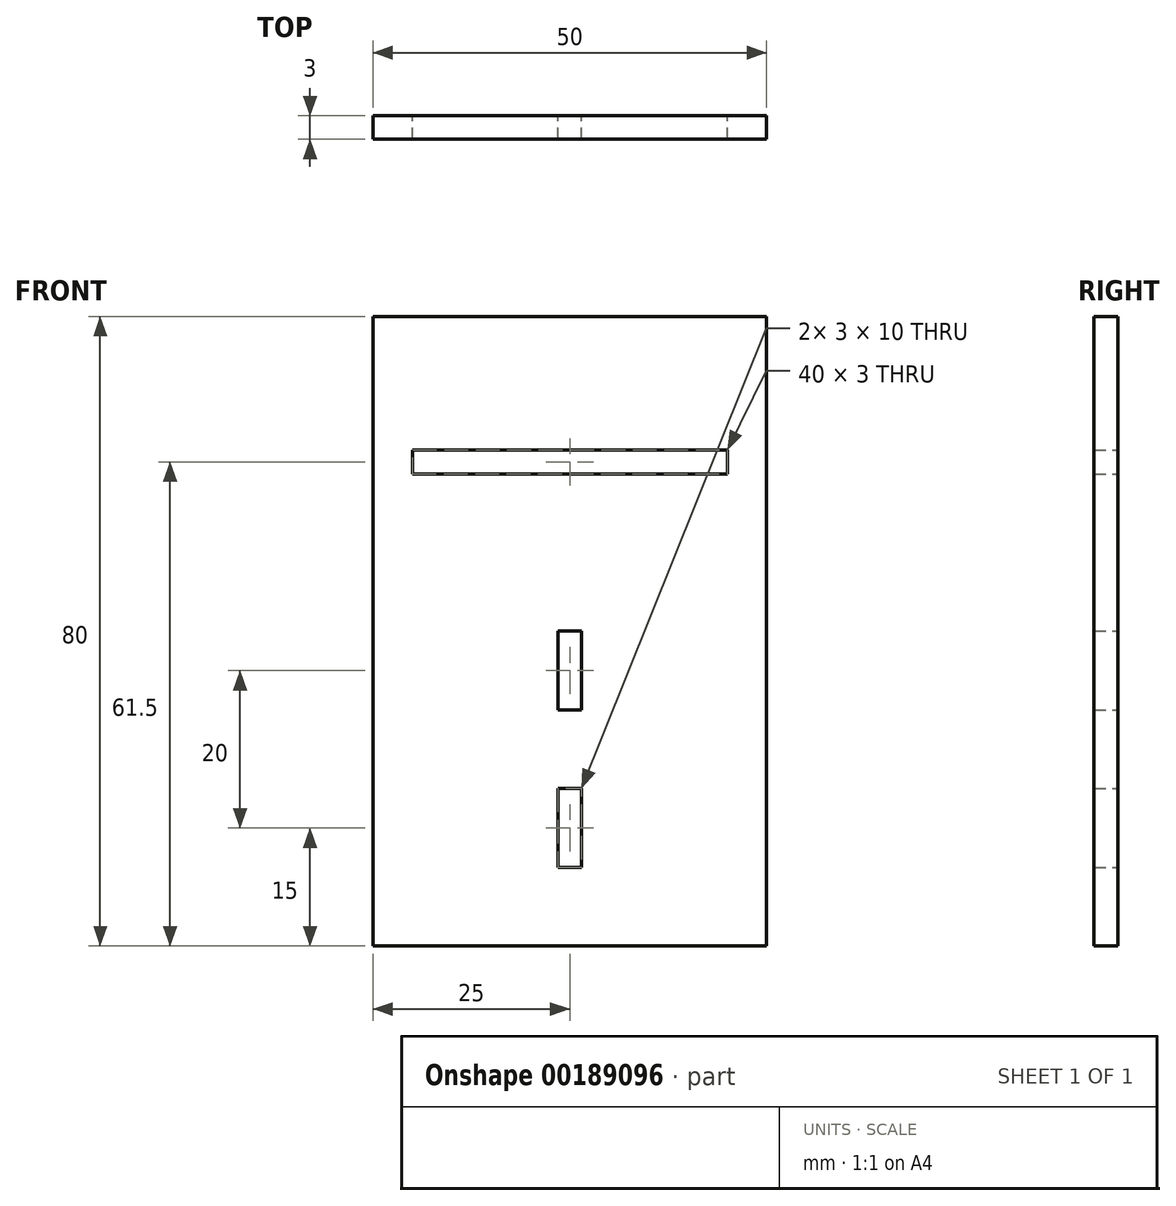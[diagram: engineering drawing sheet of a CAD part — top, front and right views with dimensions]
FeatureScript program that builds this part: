
annotation { "Feature Type Name" : "Feature", "Feature Type Description" : "" }
export const myFeature = defineFeature(function(context is Context, id is Id, definition is map)
    precondition{}
    {
        {
            var Q0;
            Q0=qCreatedBy(makeId("Front.planeOp"),FACE);
            var sketch = newSketch(context, id + "F1", { "sketchPlane" : qUnion([Q0])});
            skLineSegment(sketch, "E0.bottom", {"start": v(25, 40) * mm, "end": v(-25, 40) * mm});
            skLineSegment(sketch, "E0.top", {"start": v(25, -40) * mm, "end": v(-25, -40) * mm});
            skLineSegment(sketch, "E0.left", {"start": v(25, 40) * mm, "end": v(25, -40) * mm});
            skLineSegment(sketch, "E0.right", {"start": v(-25, 40) * mm, "end": v(-25, -40) * mm});
            skPoint(sketch, "E0.middle", {"position": v(0, 0) * mm});
            skLineSegment(sketch, "E1.bottom", {"start": v(20, 23) * mm, "end": v(-20, 23) * mm});
            skLineSegment(sketch, "E1.top", {"start": v(20, 20) * mm, "end": v(-20, 20) * mm});
            skLineSegment(sketch, "E1.left", {"start": v(20, 23) * mm, "end": v(20, 20) * mm});
            skLineSegment(sketch, "E1.right", {"start": v(-20, 23) * mm, "end": v(-20, 20) * mm});
            skPoint(sketch, "E1.middle", {"position": v(0, 21.5) * mm});
            skLineSegment(sketch, "E2.bottom", {"start": v(1.5, 0) * mm, "end": v(-1.5, 0) * mm});
            skLineSegment(sketch, "E2.top", {"start": v(1.5, -10) * mm, "end": v(-1.5, -10) * mm});
            skLineSegment(sketch, "E2.left", {"start": v(1.5, 0) * mm, "end": v(1.5, -10) * mm});
            skLineSegment(sketch, "E2.right", {"start": v(-1.5, 0) * mm, "end": v(-1.5, -10) * mm});
            skPoint(sketch, "E2.middle", {"position": v(0, -5) * mm});
            skLineSegment(sketch, "E3.bottom", {"start": v(1.5, -20) * mm, "end": v(-1.5, -20) * mm});
            skLineSegment(sketch, "E3.top", {"start": v(1.5, -30) * mm, "end": v(-1.5, -30) * mm});
            skLineSegment(sketch, "E3.left", {"start": v(1.5, -20) * mm, "end": v(1.5, -30) * mm});
            skLineSegment(sketch, "E3.right", {"start": v(-1.5, -20) * mm, "end": v(-1.5, -30) * mm});
            skPoint(sketch, "E3.middle", {"position": v(0, -25) * mm});
            skSolve(sketch);
        }
        {
            var Q0;
            Q0=makeQuery(id+"F1.imprint","IMPRINT",FACE,{"disambiguationData":[TD([[makeQuery(id+"F1.imprint","IMPRINT",EDGE,{"derivedFrom":sQuery(id+"F1.wireOp",EDGE,"E0.bottom")}),1.0]])]});
            extrude(context, id + "F0", {"entities" : qUnion([Q0]), "depth" : 3 * mm});
        }
    });
